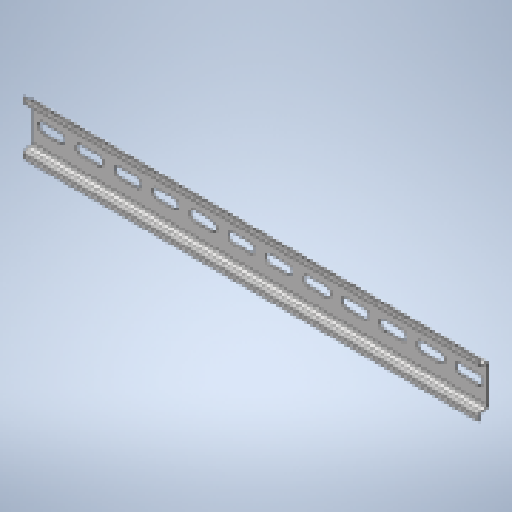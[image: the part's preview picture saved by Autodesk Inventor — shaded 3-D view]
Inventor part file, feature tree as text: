
AUTODESK INVENTOR PART (.ipt)
format: ipt  version: 2023 (Build 270158030, 158C)  size: 257,536 bytes
history: native  units: mm
features: other x4, extrude x2, sketch x2, reference x1
ambient origin geometry x8: Origin, YZ Plane, XZ Plane, XY Plane, X Axis, Y Axis, Z Axis, Center Point
bodies: Body1 (feature_tree)
feature tree (9):
  other  "DIN"
  extrude  "Extrusion1"  Depth=1.0mm
  extrude  "Extrusion2"  Depth=7.3mm
  sketch  "Sketch1"  dims[d0=1.0mm d1=1.0mm]
  reference  "Reference1"
  sketch  "Sketch2"  dims[d5=35.0mm d8=7.3mm d9=1.0mm d10=1.0mm d11=2.0mm d12=2.0mm d13=12.7mm d15=12.7mm d16=4.8mm d17=4.8mm d20=1.0mm d21=1.0mm d22=2.0mm d23=300.0mm d24=0.0mm d26=18.0mm d31=80.0mm d33=25.0mm d34=10.0mm d36=10.0mm d39=25.0mm d40=0.0mm d46=3.6mm d47=17.5mm d48=17.5mm d49=50.0mm d51=25.0mm d52=10.0mm d54=10.0mm]
  other  "<userpath>\Documents\0004-inventor\Inventor_Projects\electronics-enclosure\enclosure.iam"
  other  "enclosure.iam"
  other  "assembly-board:1"
